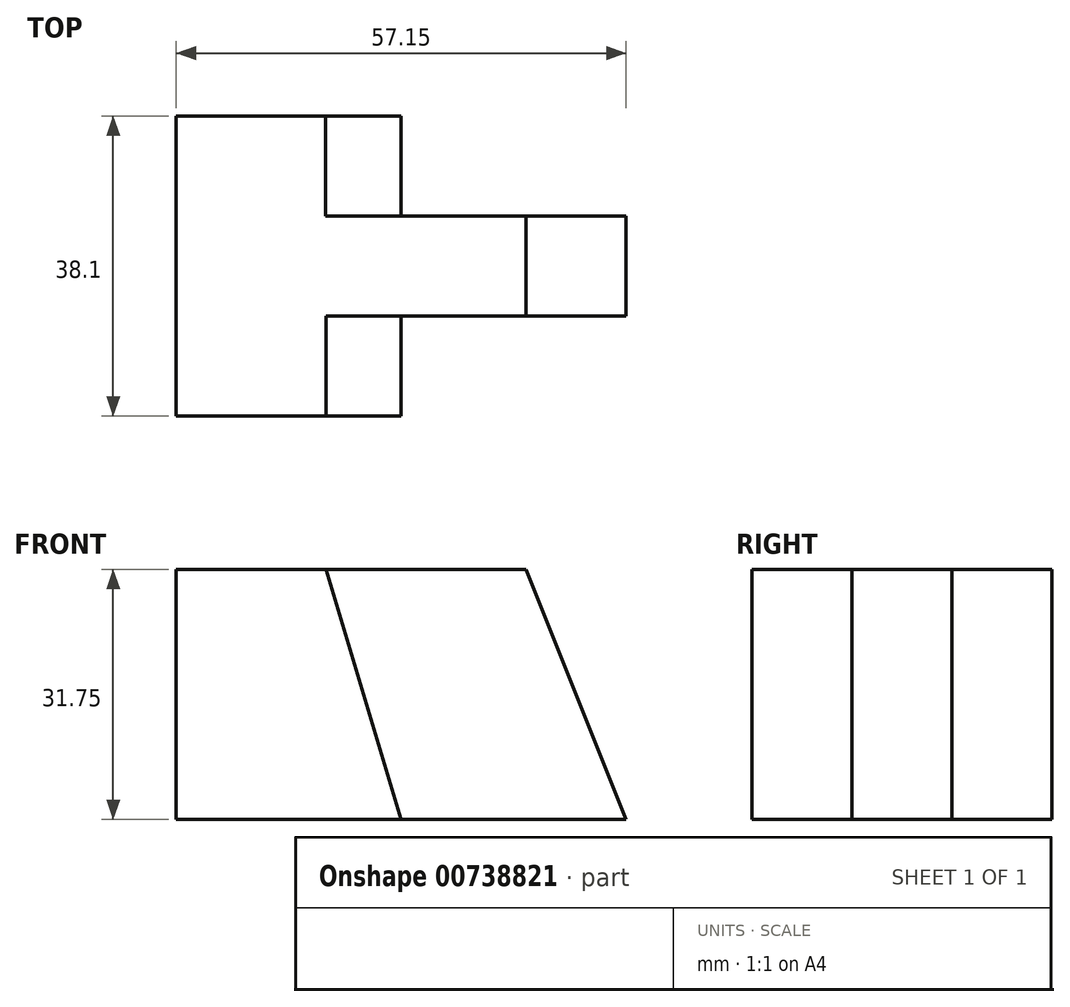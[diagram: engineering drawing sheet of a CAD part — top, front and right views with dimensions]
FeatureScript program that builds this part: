
annotation { "Feature Type Name" : "Feature", "Feature Type Description" : "" }
export const myFeature = defineFeature(function(context is Context, id is Id, definition is map)
    precondition{}
    {
        {
            var Q0;
            Q0=qCreatedBy(makeId("Front.planeOp"),FACE);
            var sketch = newSketch(context, id + "F0", { "sketchPlane" : qUnion([Q0])});
            skLineSegment(sketch, "E0", {"start": v(0, 0) * mm, "end": v(0, 31.75) * mm});
            skLineSegment(sketch, "E1", {"start": v(0, 31.75) * mm, "end": v(57.15, 31.75) * mm});
            skLineSegment(sketch, "E2", {"start": v(57.15, 31.75) * mm, "end": v(57.15, 0) * mm});
            skLineSegment(sketch, "E3", {"start": v(57.15, 0) * mm, "end": v(0, 0) * mm});
            skSolve(sketch);
        }
        {
            var Q0;
            Q0 = qSketchRegion(id + "F0", true);
            extrude(context, id + "F1", {"entities" : qUnion([Q0]), "depth" : 38.1 * mm, "offsetDistance" : 25.4 * mm});
        }
        {
            var Q0;
            Q0=makeQuery(id+"F1.opExtrude","CAP_FACE",FACE,{"disambiguationData":[OSD([sQuery(id+"F0.wireOp",EDGE,"E0"),sQuery(id+"F0.wireOp",EDGE,"E1"),sQuery(id+"F0.wireOp",EDGE,"E2"),sQuery(id+"F0.wireOp",EDGE,"E3")])],"isStart":false});
            var sketch = newSketch(context, id + "F2", { "sketchPlane" : qUnion([Q0])});
            skLineSegment(sketch, "E4", {"start": v(19.05, 31.75) * mm, "end": v(28.58, 0) * mm});
            skSolve(sketch);
        }
        {
            var Q0;
            {var subQ0=sQuery(id+"F2.wireOp",EDGE,"E4");Q0=makeQuery(id+"F2.imprint","IMPRINT",FACE,{"disambiguationData":[TD([[makeQuery(id+"F2.imprint","IMPRINT",EDGE,{"derivedFrom":subQ0}),1.0]])]});}
            extrude(context, id + "F3", {"entities" : qUnion([Q0]), "operationType" : NewBodyOperationType.REMOVE, "oppositeDirection" : true, "depth" : 12.7 * mm, "offsetDistance" : 25.4 * mm});
        }
        {
            var Q0;
            Q0=makeQuery(id+"F1.opExtrude","CAP_FACE",FACE,{"disambiguationData":[OSD([sQuery(id+"F0.wireOp",EDGE,"E0"),sQuery(id+"F0.wireOp",EDGE,"E1"),sQuery(id+"F0.wireOp",EDGE,"E2"),sQuery(id+"F0.wireOp",EDGE,"E3")])],"isStart":true});
            var sketch = newSketch(context, id + "F4", { "sketchPlane" : qUnion([Q0])});
            skLineSegment(sketch, "E5", {"start": v(-18.97, 31.75) * mm, "end": v(-28.58, 0) * mm});
            skSolve(sketch);
        }
        {
            var Q0;
            {var subQ0=sQuery(id+"F4.wireOp",EDGE,"E5");Q0=makeQuery(id+"F4.imprint","IMPRINT",FACE,{"disambiguationData":[TD([[makeQuery(id+"F4.imprint","IMPRINT",EDGE,{"derivedFrom":subQ0}),-1.0]])]});}
            extrude(context, id + "F5", {"entities" : qUnion([Q0]), "operationType" : NewBodyOperationType.REMOVE, "oppositeDirection" : true, "depth" : 12.7 * mm, "offsetDistance" : 25.4 * mm});
        }
        {
            var Q0;
            Q0=makeQuery(id+"F3.boolean.opBoolean","COPY",FACE,{"derivedFrom":makeQuery(id+"F3.opExtrude","CAP_FACE",FACE,{"disambiguationData":[OSD([sQuery(id+"F0.wireOp",EDGE,"E1"),sQuery(id+"F0.wireOp",EDGE,"E2"),sQuery(id+"F0.wireOp",EDGE,"E3"),sQuery(id+"F2.wireOp",EDGE,"E4")])],"isStart":false})});
            var sketch = newSketch(context, id + "F6", { "sketchPlane" : qUnion([Q0])});
            skLineSegment(sketch, "E6", {"start": v(57.15, 0) * mm, "end": v(44.45, 31.75) * mm});
            skSolve(sketch);
        }
        {
            var Q0;
            {var subQ0=sQuery(id+"F6.wireOp",EDGE,"E6");Q0=makeQuery(id+"F6.imprint","IMPRINT",FACE,{"disambiguationData":[TD([[makeQuery(id+"F6.imprint","IMPRINT",EDGE,{"derivedFrom":subQ0}),-1.0]])]});}
            extrude(context, id + "F7", {"entities" : qUnion([Q0]), "operationType" : NewBodyOperationType.REMOVE, "endBound" : BoundingType.THROUGH_ALL, "oppositeDirection" : true, "depth" : 25.4 * mm, "offsetDistance" : 25.4 * mm});
        }
    });
